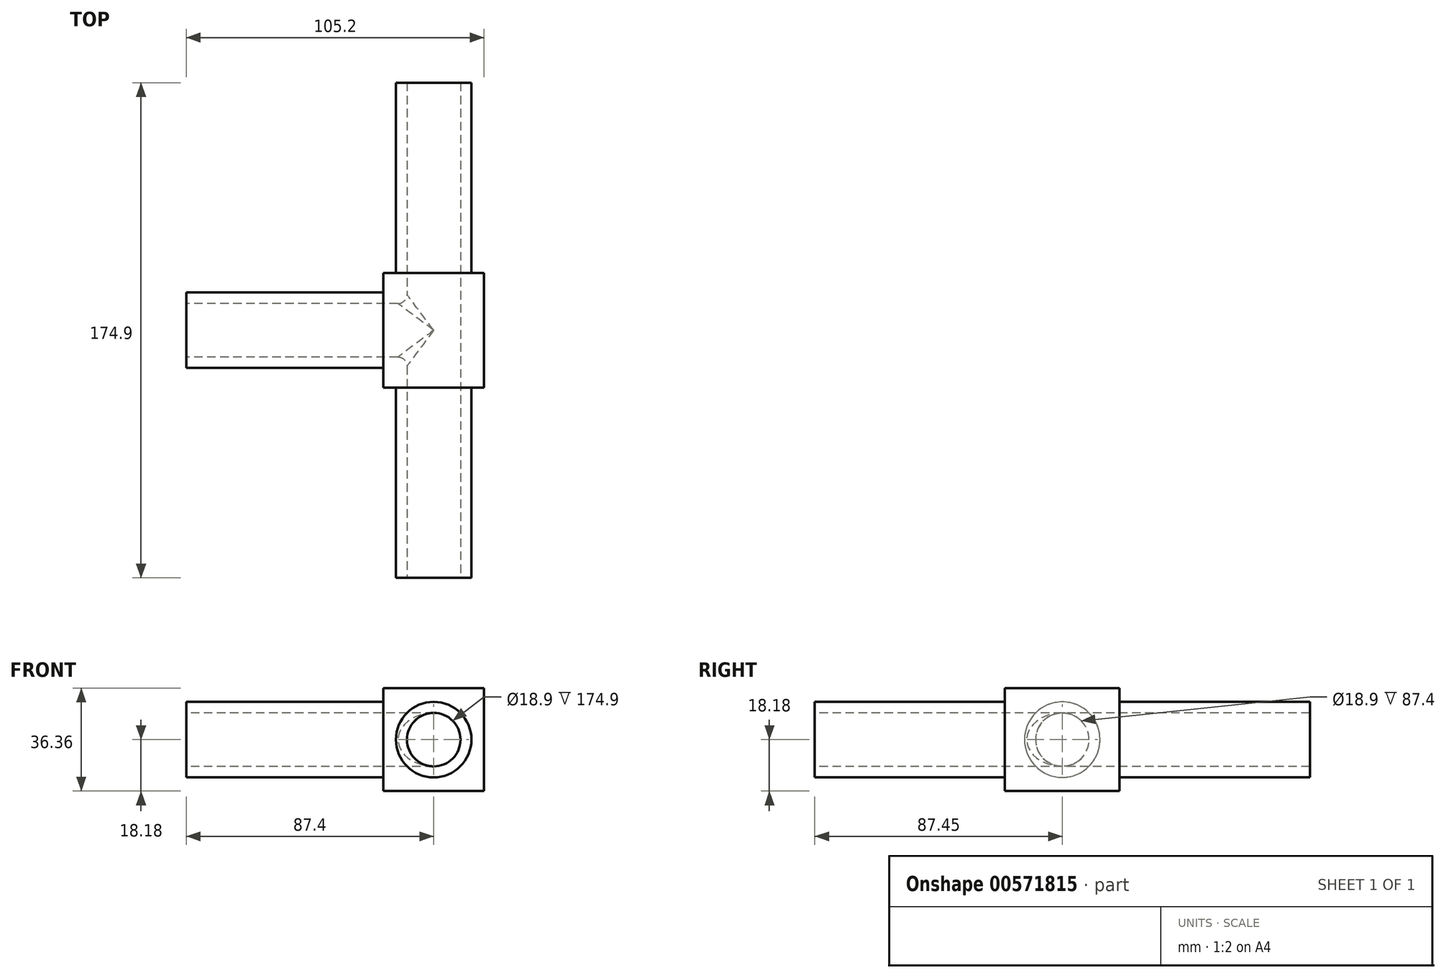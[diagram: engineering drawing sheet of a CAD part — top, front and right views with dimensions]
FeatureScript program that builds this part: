
annotation { "Feature Type Name" : "Feature", "Feature Type Description" : "" }
export const myFeature = defineFeature(function(context is Context, id is Id, definition is map)
    precondition{}
    {
        {
            var Q0;
            Q0=qCreatedBy(makeId("Front.planeOp"),FACE);
            var sketch = newSketch(context, id + "F0", { "sketchPlane" : qUnion([Q0])});
            skLineSegment(sketch, "E0.bottom", {"start": v(-17.8, -18.18) * mm, "end": v(17.8, -18.18) * mm});
            skLineSegment(sketch, "E0.top", {"start": v(-17.8, 18.18) * mm, "end": v(17.8, 18.18) * mm});
            skLineSegment(sketch, "E0.left", {"start": v(-17.8, -18.18) * mm, "end": v(-17.8, 18.18) * mm});
            skLineSegment(sketch, "E0.right", {"start": v(17.8, -18.18) * mm, "end": v(17.8, 18.18) * mm});
            skPoint(sketch, "E0.middle", {"position": v(0, 0) * mm});
            skSolve(sketch);
        }
        {
            var Q0;
            Q0=qSketchRegion(id+"F0",true);
            extrude(context, id + "F1", {"entities" : qUnion([Q0]), "endBound" : BoundingType.SYMMETRIC, "depth" : 174.9 * mm, "offsetDistance" : 25 * mm});
        }
        {
            var Q0;
            Q0=makeQuery(id+"F1.opExtrude","CAP_FACE",FACE,{"disambiguationData":[OSD([sQuery(id+"F0.wireOp",EDGE,"E0.bottom"),sQuery(id+"F0.wireOp",EDGE,"E0.top"),sQuery(id+"F0.wireOp",EDGE,"E0.left"),sQuery(id+"F0.wireOp",EDGE,"E0.right")])],"isStart":false});
            var sketch = newSketch(context, id + "F2", { "sketchPlane" : qUnion([Q0])});
            skCircle(sketch, "E1", {"center": v(0, 0) * mm, "radius": 9.45 * mm});
            skSolve(sketch);
        }
        {
            var Q0;
            Q0=qSketchRegion(id+"F2",true);
            extrude(context, id + "F3", {"entities" : qUnion([Q0]), "operationType" : NewBodyOperationType.REMOVE, "oppositeDirection" : true, "depth" : 206.4 * mm, "offsetDistance" : 25 * mm});
        }
        {
            var Q0;
            Q0=qCreatedBy(makeId("Right.planeOp"),FACE);
            var sketch = newSketch(context, id + "F4", { "sketchPlane" : qUnion([Q0])});
            skCircle(sketch, "E2", {"center": v(0, 0) * mm, "radius": 13.34 * mm});
            skSolve(sketch);
        }
        {
            var Q0;
            Q0=qSketchRegion(id+"F4",true);
            extrude(context, id + "F5", {"entities" : qUnion([Q0]), "operationType" : NewBodyOperationType.ADD, "oppositeDirection" : true, "depth" : 87.4 * mm, "offsetDistance" : 25 * mm});
        }
        {
            var Q0;
            Q0=makeQuery(id+"F5.opExtrude","CAP_FACE",FACE,{"disambiguationData":[OSD([sQuery(id+"F4.wireOp",EDGE,"E2")])],"isStart":false});
            var sketch = newSketch(context, id + "F6", { "sketchPlane" : qUnion([Q0])});
            skCircle(sketch, "E3", {"center": v(0, 0) * mm, "radius": 9.45 * mm});
            skSolve(sketch);
        }
        {
            var Q0;
            Q0=qSketchRegion(id+"F6",true);
            extrude(context, id + "F7", {"entities" : qUnion([Q0]), "operationType" : NewBodyOperationType.REMOVE, "oppositeDirection" : true, "depth" : 87.4 * mm, "offsetDistance" : 25 * mm});
        }
        {
            var Q0;
            Q0=makeQuery(id+"F1.opExtrude","CAP_FACE",FACE,{"disambiguationData":[OSD([sQuery(id+"F0.wireOp",EDGE,"E0.bottom"),sQuery(id+"F0.wireOp",EDGE,"E0.top"),sQuery(id+"F0.wireOp",EDGE,"E0.left"),sQuery(id+"F0.wireOp",EDGE,"E0.right")])],"isStart":false});
            var sketch = newSketch(context, id + "F8", { "sketchPlane" : qUnion([Q0])});
            skCircle(sketch, "E4", {"center": v(0, 0) * mm, "radius": 9.45 * mm});
            skSolve(sketch);
        }
        {
            var Q0;
            Q0=qSketchRegion(id+"F8",true);
            extrude(context, id + "F9", {"entities" : qUnion([Q0]), "operationType" : NewBodyOperationType.REMOVE, "oppositeDirection" : true, "depth" : 231.3 * mm, "offsetDistance" : 25 * mm});
        }
        {
            var Q0;
            Q0=makeQuery(id+"F9.boolean.opBoolean","INTERSECT",EDGE,{"disambiguationData":[OD(1.0)],"derivedFrom":[makeQuery(id+"F7.boolean.opBoolean","COPY",FACE,{"derivedFrom":makeQuery(id+"F7.opExtrude","SWEPT_FACE",FACE,{"disambiguationData":[OSD([sQuery(id+"F6.wireOp",EDGE,"E3")])]})}),makeQuery(id+"F9.opExtrude","SWEPT_FACE",FACE,{"disambiguationData":[OSD([sQuery(id+"F8.wireOp",EDGE,"E4")])]})]});
            var Q1;
            Q1=makeQuery(id+"F9.boolean.opBoolean","INTERSECT",EDGE,{"disambiguationData":[OD(0.0)],"derivedFrom":[makeQuery(id+"F7.boolean.opBoolean","COPY",FACE,{"derivedFrom":makeQuery(id+"F7.opExtrude","SWEPT_FACE",FACE,{"disambiguationData":[OSD([sQuery(id+"F6.wireOp",EDGE,"E3")])]})}),makeQuery(id+"F9.opExtrude","SWEPT_FACE",FACE,{"disambiguationData":[OSD([sQuery(id+"F8.wireOp",EDGE,"E4")])]})]});
            fillet(context, id + "F10", {"entities" : qUnion([Q0, Q1]), "radius" : 3.2 * mm, "tangentPropagation" : true, "allowEdgeOverflow" : false});
        }
        {
            var Q0;
            Q0=makeQuery(id+"F1.opExtrude","CAP_FACE",FACE,{"disambiguationData":[OSD([sQuery(id+"F0.wireOp",EDGE,"E0.bottom"),sQuery(id+"F0.wireOp",EDGE,"E0.top"),sQuery(id+"F0.wireOp",EDGE,"E0.left"),sQuery(id+"F0.wireOp",EDGE,"E0.right")])],"isStart":false});
            var sketch = newSketch(context, id + "F11", { "sketchPlane" : qUnion([Q0])});
            skCircle(sketch, "E5", {"center": v(0, 0) * mm, "radius": 13.34 * mm});
            skCircle(sketch, "E6", {"center": v(0, 0) * mm, "radius": 30.92 * mm});
            skSolve(sketch);
        }
        {
            var Q0;
            Q0=qSketchRegion(id+"F11",true);
            extrude(context, id + "F12", {"entities" : qUnion([Q0]), "operationType" : NewBodyOperationType.REMOVE, "oppositeDirection" : true, "depth" : 67.2 * mm, "offsetDistance" : 25 * mm});
        }
        {
            var Q0;
            Q0=makeQuery(id+"F1.opExtrude","CAP_FACE",FACE,{"disambiguationData":[OSD([sQuery(id+"F0.wireOp",EDGE,"E0.bottom"),sQuery(id+"F0.wireOp",EDGE,"E0.top"),sQuery(id+"F0.wireOp",EDGE,"E0.left"),sQuery(id+"F0.wireOp",EDGE,"E0.right")])],"isStart":true});
            var sketch = newSketch(context, id + "F13", { "sketchPlane" : qUnion([Q0])});
            skCircle(sketch, "E7", {"center": v(0, 0) * mm, "radius": 13.34 * mm});
            skCircle(sketch, "E8", {"center": v(0, 0) * mm, "radius": 36.42 * mm});
            skSolve(sketch);
        }
        {
            var Q0;
            Q0=qSketchRegion(id+"F13",true);
            extrude(context, id + "F14", {"entities" : qUnion([Q0]), "operationType" : NewBodyOperationType.REMOVE, "oppositeDirection" : true, "depth" : 67.2 * mm, "offsetDistance" : 25 * mm});
        }
    });
